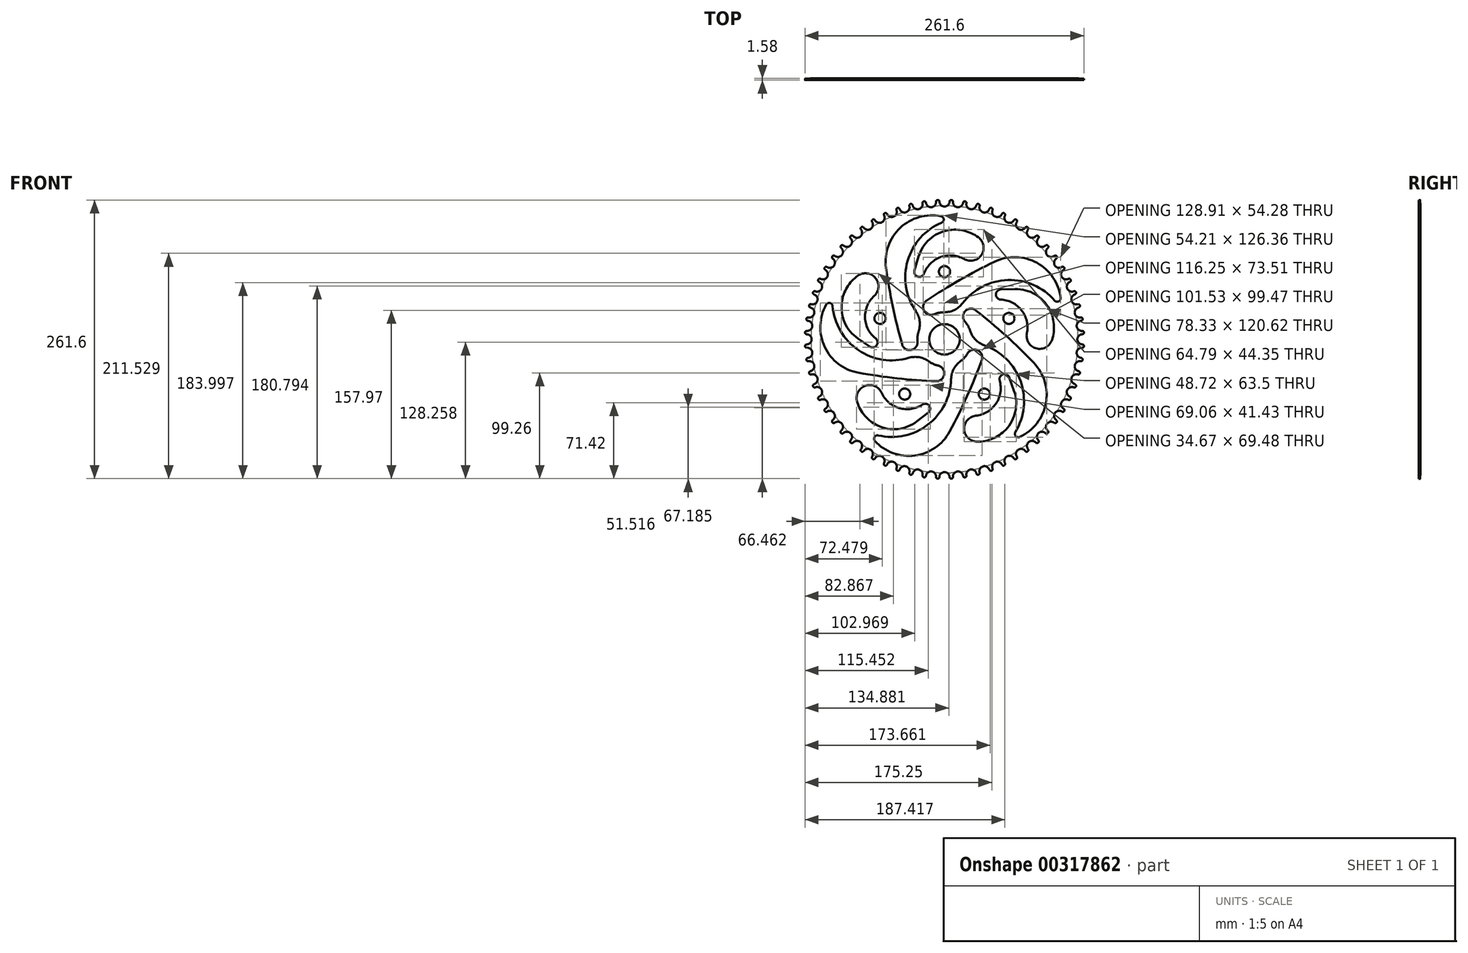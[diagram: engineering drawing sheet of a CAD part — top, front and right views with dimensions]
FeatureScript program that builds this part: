
annotation { "Feature Type Name" : "Feature", "Feature Type Description" : "" }
export const myFeature = defineFeature(function(context is Context, id is Id, definition is map)
    precondition{}
    {
        {
            var Q0;
            Q0=qCreatedBy(makeId("Front.planeOp"),FACE);
            var sketch = newSketch(context, id + "F0", { "sketchPlane" : qUnion([Q0])});
            skCircle(sketch, "E0", {"center": v(0, 0) * mm, "radius": 130.95 * mm});
            skCircle(sketch, "E1", {"center": v(0, 0) * mm, "radius": 14.29 * mm});
            skArc(sketch, "E2", {"start": v(-9.82, 23.42) * mm, "mid": v(-19.18, 26.74) * mm, "end": v(-16.8, 36.37) * mm});
            skArc(sketch, "E3", {"start": v(-16.8, 36.37) * mm, "mid": v(14.44, 55.74) * mm, "end": v(46.96, 72.85) * mm});
            skArc(sketch, "E4", {"start": v(46.96, 72.85) * mm, "mid": v(86.7, 71.8) * mm, "end": v(108.9, 38.83) * mm});
            skArc(sketch, "E5", {"start": v(108.9, 38.83) * mm, "mid": v(107.03, 35.54) * mm, "end": v(103.33, 36.37) * mm});
            skArc(sketch, "E6", {"start": v(103.33, 36.37) * mm, "mid": v(59.46, 55.67) * mm, "end": v(16.85, 33.75) * mm});
            skArc(sketch, "E7", {"start": v(16.85, 33.75) * mm, "mid": v(9.4, 27.6) * mm, "end": v(0, 25.4) * mm});
            skArc(sketch, "E8", {"start": v(0, 25.4) * mm, "mid": v(-5, 24.9) * mm, "end": v(-9.82, 23.42) * mm});
            skArc(sketch, "E9.1.0", {"start": v(-2.66, 109.51) * mm, "mid": v(-34.57, 73.76) * mm, "end": v(-26.89, 26.45) * mm});
            skArc(sketch, "E9.1.1", {"start": v(-26.89, 26.45) * mm, "mid": v(-23.34, 17.47) * mm, "end": v(-24.16, 7.85) * mm});
            skArc(sketch, "E9.1.2", {"start": v(-54.77, 67.17) * mm, "mid": v(-41.49, 104.64) * mm, "end": v(-3.27, 115.58) * mm});
            skArc(sketch, "E9.1.3", {"start": v(-25.31, -2.1) * mm, "mid": v(-31.36, -9.98) * mm, "end": v(-39.78, -4.73) * mm});
            skArc(sketch, "E9.1.4", {"start": v(-39.78, -4.73) * mm, "mid": v(-48.55, 30.96) * mm, "end": v(-54.77, 67.17) * mm});
            skArc(sketch, "E9.1.5", {"start": v(-3.27, 115.58) * mm, "mid": v(-0.73, 112.77) * mm, "end": v(-2.66, 109.51) * mm});
            skArc(sketch, "E9.1.6", {"start": v(-24.16, 7.85) * mm, "mid": v(-25.23, 2.93) * mm, "end": v(-25.31, -2.1) * mm});
            skArc(sketch, "E9.2.0", {"start": v(-104.98, 31.3) * mm, "mid": v(-80.83, -10.08) * mm, "end": v(-33.47, -17.4) * mm});
            skArc(sketch, "E9.2.1", {"start": v(-33.47, -17.4) * mm, "mid": v(-23.83, -16.8) * mm, "end": v(-14.93, -20.55) * mm});
            skArc(sketch, "E9.2.2", {"start": v(-80.8, -31.33) * mm, "mid": v(-112.34, -7.12) * mm, "end": v(-110.93, 32.6) * mm});
            skArc(sketch, "E9.2.3", {"start": v(-5.82, -24.72) * mm, "mid": v(-0.2, -32.9) * mm, "end": v(-7.8, -39.3) * mm});
            skArc(sketch, "E9.2.4", {"start": v(-7.8, -39.3) * mm, "mid": v(-44.44, -36.6) * mm, "end": v(-80.8, -31.33) * mm});
            skArc(sketch, "E9.2.5", {"start": v(-110.93, 32.6) * mm, "mid": v(-107.48, 34.16) * mm, "end": v(-104.98, 31.3) * mm});
            skArc(sketch, "E9.2.6", {"start": v(-14.93, -20.55) * mm, "mid": v(-10.58, -23.09) * mm, "end": v(-5.82, -24.72) * mm});
            skArc(sketch, "E9.3.0", {"start": v(-62.22, -90.16) * mm, "mid": v(-15.39, -79.99) * mm, "end": v(6.2, -37.2) * mm});
            skArc(sketch, "E9.3.1", {"start": v(6.2, -37.2) * mm, "mid": v(8.62, -27.86) * mm, "end": v(14.93, -20.55) * mm});
            skArc(sketch, "E9.3.2", {"start": v(4.83, -86.54) * mm, "mid": v(-27.94, -109.04) * mm, "end": v(-65.29, -95.43) * mm});
            skArc(sketch, "E9.3.3", {"start": v(21.71, -13.18) * mm, "mid": v(31.23, -10.35) * mm, "end": v(34.96, -19.56) * mm});
            skArc(sketch, "E9.3.4", {"start": v(34.96, -19.56) * mm, "mid": v(21.08, -53.58) * mm, "end": v(4.83, -86.54) * mm});
            skArc(sketch, "E9.3.5", {"start": v(-65.29, -95.43) * mm, "mid": v(-65.7, -91.66) * mm, "end": v(-62.22, -90.16) * mm});
            skArc(sketch, "E9.3.6", {"start": v(14.93, -20.55) * mm, "mid": v(18.69, -17.2) * mm, "end": v(21.71, -13.18) * mm});
            skArc(sketch, "E9.4.0", {"start": v(66.52, -87.03) * mm, "mid": v(71.32, -39.35) * mm, "end": v(37.3, -5.6) * mm});
            skArc(sketch, "E9.4.1", {"start": v(37.3, -5.6) * mm, "mid": v(29.16, -0.41) * mm, "end": v(24.16, 7.85) * mm});
            skArc(sketch, "E9.4.2", {"start": v(83.8, -22.15) * mm, "mid": v(95.07, -60.27) * mm, "end": v(70.58, -91.58) * mm});
            skArc(sketch, "E9.4.3", {"start": v(19.24, 16.58) * mm, "mid": v(19.5, 26.5) * mm, "end": v(29.4, 27.2) * mm});
            skArc(sketch, "E9.4.4", {"start": v(29.4, 27.2) * mm, "mid": v(57.47, 3.5) * mm, "end": v(83.8, -22.15) * mm});
            skArc(sketch, "E9.4.5", {"start": v(70.58, -91.58) * mm, "mid": v(66.87, -90.8) * mm, "end": v(66.52, -87.03) * mm});
            skArc(sketch, "E9.4.6", {"start": v(24.16, 7.85) * mm, "mid": v(22.13, 12.46) * mm, "end": v(19.24, 16.58) * mm});
            skArc(sketch, "E10", {"start": v(3.39, 102.34) * mm, "mid": v(-14.01, 93.86) * mm, "end": v(-24.34, 77.5) * mm});
            skArc(sketch, "E11", {"start": v(3.39, 102.34) * mm, "mid": v(18.22, 101.96) * mm, "end": v(31.69, 95.75) * mm});
            skArc(sketch, "E12", {"start": v(31.69, 95.75) * mm, "mid": v(34.69, 79.22) * mm, "end": v(18.36, 75.29) * mm});
            skArc(sketch, "E13", {"start": v(18.36, 75.29) * mm, "mid": v(-3.6, 77.18) * mm, "end": v(-19.22, 61.62) * mm});
            skArc(sketch, "E14", {"start": v(-19.22, 61.62) * mm, "mid": v(-25.11, 58.78) * mm, "end": v(-28.14, 64.57) * mm});
            skLineSegment(sketch, "E15", {"start": v(-28.14, 64.57) * mm, "end": v(-24.34, 77.5) * mm});
            skArc(sketch, "E16.1.1", {"start": v(-65.93, 40.72) * mm, "mid": v(-74.51, 20.42) * mm, "end": v(-64.55, 0.76) * mm});
            skArc(sketch, "E16.1.2", {"start": v(-81.27, 59.73) * mm, "mid": v(-64.63, 57.47) * mm, "end": v(-65.93, 40.72) * mm});
            skArc(sketch, "E16.1.3", {"start": v(-96.29, 34.85) * mm, "mid": v(-91.34, 48.83) * mm, "end": v(-81.27, 59.73) * mm});
            skArc(sketch, "E16.1.4", {"start": v(-96.29, 34.85) * mm, "mid": v(-93.6, 15.68) * mm, "end": v(-81.22, 0.8) * mm});
            skLineSegment(sketch, "E16.1.5", {"start": v(-70.1, -6.81) * mm, "end": v(-81.22, 0.8) * mm});
            skArc(sketch, "E16.1.6", {"start": v(-64.55, 0.76) * mm, "mid": v(-63.66, -5.72) * mm, "end": v(-70.1, -6.81) * mm});
            skArc(sketch, "E16.2.1", {"start": v(-59.1, -50.12) * mm, "mid": v(-42.45, -64.56) * mm, "end": v(-20.67, -61.15) * mm});
            skArc(sketch, "E16.2.2", {"start": v(-81.92, -58.84) * mm, "mid": v(-74.63, -43.7) * mm, "end": v(-59.1, -50.12) * mm});
            skArc(sketch, "E16.2.3", {"start": v(-62.9, -80.8) * mm, "mid": v(-74.67, -71.78) * mm, "end": v(-81.92, -58.84) * mm});
            skArc(sketch, "E16.2.4", {"start": v(-62.9, -80.8) * mm, "mid": v(-43.84, -84.17) * mm, "end": v(-25.85, -77) * mm});
            skLineSegment(sketch, "E16.2.5", {"start": v(-15.18, -68.78) * mm, "end": v(-25.85, -77) * mm});
            skArc(sketch, "E16.2.6", {"start": v(-20.67, -61.15) * mm, "mid": v(-14.24, -62.32) * mm, "end": v(-15.18, -68.78) * mm});
            skArc(sketch, "E16.3.1", {"start": v(29.4, -71.7) * mm, "mid": v(48.28, -60.32) * mm, "end": v(51.77, -38.55) * mm});
            skArc(sketch, "E16.3.2", {"start": v(30.64, -96.1) * mm, "mid": v(18.5, -84.48) * mm, "end": v(29.4, -71.7) * mm});
            skArc(sketch, "E16.3.3", {"start": v(57.41, -84.8) * mm, "mid": v(45.2, -93.2) * mm, "end": v(30.64, -96.1) * mm});
            skArc(sketch, "E16.3.4", {"start": v(57.41, -84.8) * mm, "mid": v(66.5, -67.7) * mm, "end": v(65.24, -48.38) * mm});
            skLineSegment(sketch, "E16.3.5", {"start": v(60.72, -35.7) * mm, "end": v(65.24, -48.38) * mm});
            skArc(sketch, "E16.3.6", {"start": v(51.77, -38.55) * mm, "mid": v(54.87, -32.8) * mm, "end": v(60.72, -35.7) * mm});
            skCircle(sketch, "E16.4.0", {"center": v(60.4, 19.62) * mm, "radius": 5.24 * mm});
            skArc(sketch, "E16.4.1", {"start": v(77.27, 5.8) * mm, "mid": v(72.28, 27.28) * mm, "end": v(52.66, 37.32) * mm});
            skArc(sketch, "E16.4.2", {"start": v(100.86, -0.55) * mm, "mid": v(86.06, -8.5) * mm, "end": v(77.27, 5.8) * mm});
            skArc(sketch, "E16.4.3", {"start": v(98.38, 28.4) * mm, "mid": v(102.6, 14.18) * mm, "end": v(100.86, -0.55) * mm});
            skArc(sketch, "E16.4.4", {"start": v(98.38, 28.4) * mm, "mid": v(84.94, 42.33) * mm, "end": v(66.18, 47.1) * mm});
            skLineSegment(sketch, "E16.4.5", {"start": v(52.71, 46.72) * mm, "end": v(66.18, 47.1) * mm});
            skArc(sketch, "E16.4.6", {"start": v(52.66, 37.32) * mm, "mid": v(48.15, 42.05) * mm, "end": v(52.71, 46.72) * mm});
            skArc(sketch, "E17", {"start": v(129.27, 4.76) * mm, "mid": v(125.86, -3.23) * mm, "end": v(134.1, -0.46) * mm});
            skArc(sketch, "E18", {"start": v(129.27, 4.76) * mm, "mid": v(130.82, 6.43) * mm, "end": v(129.12, 7.94) * mm});
            skLineSegment(sketch, "E19", {"start": v(129.12, 7.94) * mm, "end": v(137.96, 11.37) * mm});
            skLineSegment(sketch, "E20", {"start": v(137.96, 11.37) * mm, "end": v(139.02, 0) * mm});
            skLineSegment(sketch, "E21", {"start": v(139.02, 0) * mm, "end": v(134.1, -0.46) * mm});
            skLineSegment(sketch, "E22.1.0", {"start": v(127.72, 20.55) * mm, "end": v(136.19, 24.83) * mm});
            skLineSegment(sketch, "E22.1.1", {"start": v(136.19, 24.83) * mm, "end": v(138.35, 13.63) * mm});
            skLineSegment(sketch, "E22.1.2", {"start": v(138.35, 13.63) * mm, "end": v(133.5, 12.69) * mm});
            skArc(sketch, "E22.1.3", {"start": v(128.18, 17.4) * mm, "mid": v(129.56, 19.22) * mm, "end": v(127.72, 20.55) * mm});
            skArc(sketch, "E22.1.4", {"start": v(128.18, 17.4) * mm, "mid": v(125.58, 9.12) * mm, "end": v(133.5, 12.69) * mm});
            skLineSegment(sketch, "E22.2.0", {"start": v(125.09, 32.97) * mm, "end": v(133.1, 38.06) * mm});
            skLineSegment(sketch, "E22.2.1", {"start": v(133.1, 38.06) * mm, "end": v(136.35, 27.12) * mm});
            skLineSegment(sketch, "E22.2.2", {"start": v(136.35, 27.12) * mm, "end": v(131.61, 25.71) * mm});
            skArc(sketch, "E22.2.3", {"start": v(125.86, 29.9) * mm, "mid": v(127.05, 31.83) * mm, "end": v(125.09, 32.97) * mm});
            skArc(sketch, "E22.2.4", {"start": v(125.86, 29.9) * mm, "mid": v(124.08, 21.38) * mm, "end": v(131.61, 25.71) * mm});
            skLineSegment(sketch, "E22.3.0", {"start": v(121.25, 45.08) * mm, "end": v(128.72, 50.93) * mm});
            skLineSegment(sketch, "E22.3.1", {"start": v(128.72, 50.93) * mm, "end": v(133.04, 40.36) * mm});
            skLineSegment(sketch, "E22.3.2", {"start": v(133.04, 40.36) * mm, "end": v(128.46, 38.49) * mm});
            skArc(sketch, "E22.3.3", {"start": v(122.32, 42.08) * mm, "mid": v(123.32, 44.13) * mm, "end": v(121.25, 45.08) * mm});
            skArc(sketch, "E22.3.4", {"start": v(122.32, 42.08) * mm, "mid": v(121.38, 33.44) * mm, "end": v(128.46, 38.49) * mm});
            skLineSegment(sketch, "E22.4.0", {"start": v(116.25, 56.74) * mm, "end": v(123.11, 63.3) * mm});
            skLineSegment(sketch, "E22.4.1", {"start": v(123.11, 63.3) * mm, "end": v(128.44, 53.2) * mm});
            skLineSegment(sketch, "E22.4.2", {"start": v(128.44, 53.2) * mm, "end": v(124.07, 50.9) * mm});
            skArc(sketch, "E22.4.3", {"start": v(117.61, 53.87) * mm, "mid": v(118.4, 56) * mm, "end": v(116.25, 56.74) * mm});
            skArc(sketch, "E22.4.4", {"start": v(117.61, 53.87) * mm, "mid": v(117.52, 45.18) * mm, "end": v(124.07, 50.9) * mm});
            skLineSegment(sketch, "E22.5.0", {"start": v(110.13, 67.87) * mm, "end": v(116.32, 75.06) * mm});
            skLineSegment(sketch, "E22.5.1", {"start": v(116.32, 75.06) * mm, "end": v(122.6, 65.54) * mm});
            skLineSegment(sketch, "E22.5.2", {"start": v(122.6, 65.54) * mm, "end": v(118.48, 62.81) * mm});
            skArc(sketch, "E22.5.3", {"start": v(111.76, 65.14) * mm, "mid": v(112.34, 67.34) * mm, "end": v(110.13, 67.87) * mm});
            skArc(sketch, "E22.5.4", {"start": v(111.76, 65.14) * mm, "mid": v(112.53, 56.48) * mm, "end": v(118.48, 62.81) * mm});
            skLineSegment(sketch, "E22.6.0", {"start": v(102.95, 78.33) * mm, "end": v(108.4, 86.1) * mm});
            skLineSegment(sketch, "E22.6.1", {"start": v(108.4, 86.1) * mm, "end": v(115.6, 77.24) * mm});
            skLineSegment(sketch, "E22.6.2", {"start": v(115.6, 77.24) * mm, "end": v(111.76, 74.12) * mm});
            skArc(sketch, "E22.6.3", {"start": v(104.84, 75.78) * mm, "mid": v(105.2, 78.02) * mm, "end": v(102.95, 78.33) * mm});
            skArc(sketch, "E22.6.4", {"start": v(104.84, 75.78) * mm, "mid": v(106.45, 67.24) * mm, "end": v(111.76, 74.12) * mm});
            skLineSegment(sketch, "E22.7.0", {"start": v(94.77, 88.05) * mm, "end": v(99.44, 96.3) * mm});
            skLineSegment(sketch, "E22.7.1", {"start": v(99.44, 96.3) * mm, "end": v(107.47, 88.2) * mm});
            skLineSegment(sketch, "E22.7.2", {"start": v(107.47, 88.2) * mm, "end": v(103.95, 84.72) * mm});
            skArc(sketch, "E22.7.3", {"start": v(96.9, 85.7) * mm, "mid": v(97.04, 87.96) * mm, "end": v(94.77, 88.05) * mm});
            skArc(sketch, "E22.7.4", {"start": v(96.9, 85.7) * mm, "mid": v(99.35, 77.35) * mm, "end": v(103.95, 84.72) * mm});
            skLineSegment(sketch, "E22.8.0", {"start": v(85.69, 96.91) * mm, "end": v(89.52, 105.6) * mm});
            skLineSegment(sketch, "E22.8.1", {"start": v(89.52, 105.6) * mm, "end": v(98.3, 98.3) * mm});
            skLineSegment(sketch, "E22.8.2", {"start": v(98.3, 98.3) * mm, "end": v(95.15, 94.5) * mm});
            skArc(sketch, "E22.8.3", {"start": v(88.04, 94.78) * mm, "mid": v(87.96, 97.05) * mm, "end": v(85.69, 96.91) * mm});
            skArc(sketch, "E22.8.4", {"start": v(88.04, 94.78) * mm, "mid": v(91.29, 86.71) * mm, "end": v(95.15, 94.5) * mm});
            skLineSegment(sketch, "E22.9.0", {"start": v(75.78, 104.84) * mm, "end": v(78.74, 113.86) * mm});
            skLineSegment(sketch, "E22.9.1", {"start": v(78.74, 113.86) * mm, "end": v(88.2, 107.47) * mm});
            skLineSegment(sketch, "E22.9.2", {"start": v(88.2, 107.47) * mm, "end": v(85.43, 103.37) * mm});
            skArc(sketch, "E22.9.3", {"start": v(78.33, 102.95) * mm, "mid": v(78.02, 105.2) * mm, "end": v(75.78, 104.84) * mm});
            skArc(sketch, "E22.9.4", {"start": v(78.33, 102.95) * mm, "mid": v(82.35, 95.24) * mm, "end": v(85.43, 103.37) * mm});
            skLineSegment(sketch, "E22.10.0", {"start": v(65.13, 111.77) * mm, "end": v(67.2, 121.03) * mm});
            skLineSegment(sketch, "E22.10.1", {"start": v(67.2, 121.03) * mm, "end": v(77.24, 115.6) * mm});
            skLineSegment(sketch, "E22.10.2", {"start": v(77.24, 115.6) * mm, "end": v(74.88, 111.25) * mm});
            skArc(sketch, "E22.10.3", {"start": v(67.86, 110.13) * mm, "mid": v(67.33, 112.34) * mm, "end": v(65.13, 111.77) * mm});
            skArc(sketch, "E22.10.4", {"start": v(67.86, 110.13) * mm, "mid": v(72.62, 102.86) * mm, "end": v(74.88, 111.25) * mm});
            skLineSegment(sketch, "E22.11.0", {"start": v(53.87, 117.61) * mm, "end": v(55.01, 127.03) * mm});
            skLineSegment(sketch, "E22.11.1", {"start": v(55.01, 127.03) * mm, "end": v(65.54, 122.6) * mm});
            skLineSegment(sketch, "E22.11.2", {"start": v(65.54, 122.6) * mm, "end": v(63.62, 118.05) * mm});
            skArc(sketch, "E22.11.3", {"start": v(56.74, 116.25) * mm, "mid": v(56, 118.4) * mm, "end": v(53.87, 117.61) * mm});
            skArc(sketch, "E22.11.4", {"start": v(56.74, 116.25) * mm, "mid": v(62.18, 109.48) * mm, "end": v(63.62, 118.05) * mm});
            skLineSegment(sketch, "E22.12.0", {"start": v(42.08, 122.33) * mm, "end": v(42.3, 131.81) * mm});
            skLineSegment(sketch, "E22.12.1", {"start": v(42.3, 131.81) * mm, "end": v(53.2, 128.44) * mm});
            skLineSegment(sketch, "E22.12.2", {"start": v(53.2, 128.44) * mm, "end": v(51.74, 123.72) * mm});
            skArc(sketch, "E22.12.3", {"start": v(45.07, 121.26) * mm, "mid": v(44.12, 123.32) * mm, "end": v(42.08, 122.33) * mm});
            skArc(sketch, "E22.12.4", {"start": v(45.07, 121.26) * mm, "mid": v(51.15, 115.05) * mm, "end": v(51.74, 123.72) * mm});
            skLineSegment(sketch, "E22.13.0", {"start": v(29.89, 125.86) * mm, "end": v(29.17, 135.32) * mm});
            skLineSegment(sketch, "E22.13.1", {"start": v(29.17, 135.32) * mm, "end": v(40.36, 133.04) * mm});
            skLineSegment(sketch, "E22.13.2", {"start": v(40.36, 133.04) * mm, "end": v(39.37, 128.2) * mm});
            skArc(sketch, "E22.13.3", {"start": v(32.97, 125.09) * mm, "mid": v(31.82, 127.05) * mm, "end": v(29.89, 125.86) * mm});
            skArc(sketch, "E22.13.4", {"start": v(32.97, 125.09) * mm, "mid": v(39.63, 119.5) * mm, "end": v(39.37, 128.2) * mm});
            skLineSegment(sketch, "E22.14.0", {"start": v(17.4, 128.18) * mm, "end": v(15.77, 137.53) * mm});
            skLineSegment(sketch, "E22.14.1", {"start": v(15.77, 137.53) * mm, "end": v(27.12, 136.35) * mm});
            skLineSegment(sketch, "E22.14.2", {"start": v(27.12, 136.35) * mm, "end": v(26.61, 131.44) * mm});
            skArc(sketch, "E22.14.3", {"start": v(20.55, 127.72) * mm, "mid": v(19.22, 129.56) * mm, "end": v(17.4, 128.18) * mm});
            skArc(sketch, "E22.14.4", {"start": v(20.55, 127.72) * mm, "mid": v(27.73, 122.82) * mm, "end": v(26.61, 131.44) * mm});
            skLineSegment(sketch, "E22.15.0", {"start": v(4.76, 129.27) * mm, "end": v(2.21, 138.41) * mm});
            skLineSegment(sketch, "E22.15.1", {"start": v(2.21, 138.41) * mm, "end": v(13.63, 138.35) * mm});
            skLineSegment(sketch, "E22.15.2", {"start": v(13.63, 138.35) * mm, "end": v(13.6, 133.41) * mm});
            skArc(sketch, "E22.15.3", {"start": v(7.93, 129.12) * mm, "mid": v(6.42, 130.82) * mm, "end": v(4.76, 129.27) * mm});
            skArc(sketch, "E22.15.4", {"start": v(7.93, 129.12) * mm, "mid": v(15.56, 124.94) * mm, "end": v(13.6, 133.41) * mm});
            skLineSegment(sketch, "E22.16.0", {"start": v(-7.94, 129.12) * mm, "end": v(-11.37, 137.96) * mm});
            skLineSegment(sketch, "E22.16.1", {"start": v(-11.37, 137.96) * mm, "end": v(0, 139.02) * mm});
            skLineSegment(sketch, "E22.16.2", {"start": v(0, 139.02) * mm, "end": v(0.46, 134.1) * mm});
            skArc(sketch, "E22.16.3", {"start": v(-4.76, 129.27) * mm, "mid": v(-6.43, 130.82) * mm, "end": v(-7.94, 129.12) * mm});
            skArc(sketch, "E22.16.4", {"start": v(-4.76, 129.27) * mm, "mid": v(3.23, 125.86) * mm, "end": v(0.46, 134.1) * mm});
            skLineSegment(sketch, "E22.17.0", {"start": v(-20.55, 127.72) * mm, "end": v(-24.83, 136.19) * mm});
            skLineSegment(sketch, "E22.17.1", {"start": v(-24.83, 136.19) * mm, "end": v(-13.63, 138.35) * mm});
            skLineSegment(sketch, "E22.17.2", {"start": v(-13.63, 138.35) * mm, "end": v(-12.69, 133.5) * mm});
            skArc(sketch, "E22.17.3", {"start": v(-17.4, 128.18) * mm, "mid": v(-19.22, 129.56) * mm, "end": v(-20.55, 127.72) * mm});
            skArc(sketch, "E22.17.4", {"start": v(-17.4, 128.18) * mm, "mid": v(-9.12, 125.58) * mm, "end": v(-12.69, 133.5) * mm});
            skLineSegment(sketch, "E22.18.0", {"start": v(-32.97, 125.09) * mm, "end": v(-38.06, 133.1) * mm});
            skLineSegment(sketch, "E22.18.1", {"start": v(-38.06, 133.1) * mm, "end": v(-27.12, 136.35) * mm});
            skLineSegment(sketch, "E22.18.2", {"start": v(-27.12, 136.35) * mm, "end": v(-25.71, 131.61) * mm});
            skArc(sketch, "E22.18.3", {"start": v(-29.9, 125.86) * mm, "mid": v(-31.83, 127.05) * mm, "end": v(-32.97, 125.09) * mm});
            skArc(sketch, "E22.18.4", {"start": v(-29.9, 125.86) * mm, "mid": v(-21.38, 124.08) * mm, "end": v(-25.71, 131.61) * mm});
            skLineSegment(sketch, "E22.19.0", {"start": v(-45.08, 121.25) * mm, "end": v(-50.93, 128.72) * mm});
            skLineSegment(sketch, "E22.19.1", {"start": v(-50.93, 128.72) * mm, "end": v(-40.36, 133.04) * mm});
            skLineSegment(sketch, "E22.19.2", {"start": v(-40.36, 133.04) * mm, "end": v(-38.49, 128.46) * mm});
            skArc(sketch, "E22.19.3", {"start": v(-42.08, 122.32) * mm, "mid": v(-44.13, 123.32) * mm, "end": v(-45.08, 121.25) * mm});
            skArc(sketch, "E22.19.4", {"start": v(-42.08, 122.32) * mm, "mid": v(-33.44, 121.38) * mm, "end": v(-38.49, 128.46) * mm});
            skLineSegment(sketch, "E22.20.0", {"start": v(-56.74, 116.25) * mm, "end": v(-63.3, 123.11) * mm});
            skLineSegment(sketch, "E22.20.1", {"start": v(-63.3, 123.11) * mm, "end": v(-53.2, 128.44) * mm});
            skLineSegment(sketch, "E22.20.2", {"start": v(-53.2, 128.44) * mm, "end": v(-50.9, 124.07) * mm});
            skArc(sketch, "E22.20.3", {"start": v(-53.87, 117.61) * mm, "mid": v(-56, 118.4) * mm, "end": v(-56.74, 116.25) * mm});
            skArc(sketch, "E22.20.4", {"start": v(-53.87, 117.61) * mm, "mid": v(-45.18, 117.52) * mm, "end": v(-50.9, 124.07) * mm});
            skLineSegment(sketch, "E22.21.0", {"start": v(-67.87, 110.13) * mm, "end": v(-75.06, 116.32) * mm});
            skLineSegment(sketch, "E22.21.1", {"start": v(-75.06, 116.32) * mm, "end": v(-65.54, 122.6) * mm});
            skLineSegment(sketch, "E22.21.2", {"start": v(-65.54, 122.6) * mm, "end": v(-62.81, 118.48) * mm});
            skArc(sketch, "E22.21.3", {"start": v(-65.14, 111.76) * mm, "mid": v(-67.34, 112.34) * mm, "end": v(-67.87, 110.13) * mm});
            skArc(sketch, "E22.21.4", {"start": v(-65.14, 111.76) * mm, "mid": v(-56.48, 112.53) * mm, "end": v(-62.81, 118.48) * mm});
            skLineSegment(sketch, "E22.22.0", {"start": v(-78.33, 102.95) * mm, "end": v(-86.1, 108.4) * mm});
            skLineSegment(sketch, "E22.22.1", {"start": v(-86.1, 108.4) * mm, "end": v(-77.24, 115.6) * mm});
            skLineSegment(sketch, "E22.22.2", {"start": v(-77.24, 115.6) * mm, "end": v(-74.12, 111.76) * mm});
            skArc(sketch, "E22.22.3", {"start": v(-75.78, 104.84) * mm, "mid": v(-78.02, 105.2) * mm, "end": v(-78.33, 102.95) * mm});
            skArc(sketch, "E22.22.4", {"start": v(-75.78, 104.84) * mm, "mid": v(-67.24, 106.45) * mm, "end": v(-74.12, 111.76) * mm});
            skLineSegment(sketch, "E22.23.0", {"start": v(-88.05, 94.77) * mm, "end": v(-96.3, 99.44) * mm});
            skLineSegment(sketch, "E22.23.1", {"start": v(-96.3, 99.44) * mm, "end": v(-88.2, 107.47) * mm});
            skLineSegment(sketch, "E22.23.2", {"start": v(-88.2, 107.47) * mm, "end": v(-84.72, 103.95) * mm});
            skArc(sketch, "E22.23.3", {"start": v(-85.7, 96.9) * mm, "mid": v(-87.96, 97.04) * mm, "end": v(-88.05, 94.77) * mm});
            skArc(sketch, "E22.23.4", {"start": v(-85.7, 96.9) * mm, "mid": v(-77.35, 99.35) * mm, "end": v(-84.72, 103.95) * mm});
            skLineSegment(sketch, "E22.24.0", {"start": v(-96.91, 85.69) * mm, "end": v(-105.6, 89.52) * mm});
            skLineSegment(sketch, "E22.24.1", {"start": v(-105.6, 89.52) * mm, "end": v(-98.3, 98.3) * mm});
            skLineSegment(sketch, "E22.24.2", {"start": v(-98.3, 98.3) * mm, "end": v(-94.5, 95.15) * mm});
            skArc(sketch, "E22.24.3", {"start": v(-94.78, 88.04) * mm, "mid": v(-97.05, 87.96) * mm, "end": v(-96.91, 85.69) * mm});
            skArc(sketch, "E22.24.4", {"start": v(-94.78, 88.04) * mm, "mid": v(-86.71, 91.29) * mm, "end": v(-94.5, 95.15) * mm});
            skLineSegment(sketch, "E22.25.0", {"start": v(-104.84, 75.78) * mm, "end": v(-113.86, 78.74) * mm});
            skLineSegment(sketch, "E22.25.1", {"start": v(-113.86, 78.74) * mm, "end": v(-107.47, 88.2) * mm});
            skLineSegment(sketch, "E22.25.2", {"start": v(-107.47, 88.2) * mm, "end": v(-103.37, 85.43) * mm});
            skArc(sketch, "E22.25.3", {"start": v(-102.95, 78.33) * mm, "mid": v(-105.2, 78.02) * mm, "end": v(-104.84, 75.78) * mm});
            skArc(sketch, "E22.25.4", {"start": v(-102.95, 78.33) * mm, "mid": v(-95.24, 82.35) * mm, "end": v(-103.37, 85.43) * mm});
            skLineSegment(sketch, "E22.26.0", {"start": v(-111.77, 65.13) * mm, "end": v(-121.03, 67.2) * mm});
            skLineSegment(sketch, "E22.26.1", {"start": v(-121.03, 67.2) * mm, "end": v(-115.6, 77.24) * mm});
            skLineSegment(sketch, "E22.26.2", {"start": v(-115.6, 77.24) * mm, "end": v(-111.25, 74.88) * mm});
            skArc(sketch, "E22.26.3", {"start": v(-110.13, 67.86) * mm, "mid": v(-112.34, 67.33) * mm, "end": v(-111.77, 65.13) * mm});
            skArc(sketch, "E22.26.4", {"start": v(-110.13, 67.86) * mm, "mid": v(-102.86, 72.62) * mm, "end": v(-111.25, 74.88) * mm});
            skLineSegment(sketch, "E22.27.0", {"start": v(-117.61, 53.87) * mm, "end": v(-127.03, 55.01) * mm});
            skLineSegment(sketch, "E22.27.1", {"start": v(-127.03, 55.01) * mm, "end": v(-122.6, 65.54) * mm});
            skLineSegment(sketch, "E22.27.2", {"start": v(-122.6, 65.54) * mm, "end": v(-118.05, 63.62) * mm});
            skArc(sketch, "E22.27.3", {"start": v(-116.25, 56.74) * mm, "mid": v(-118.4, 56) * mm, "end": v(-117.61, 53.87) * mm});
            skArc(sketch, "E22.27.4", {"start": v(-116.25, 56.74) * mm, "mid": v(-109.48, 62.18) * mm, "end": v(-118.05, 63.62) * mm});
            skLineSegment(sketch, "E22.28.0", {"start": v(-122.33, 42.08) * mm, "end": v(-131.81, 42.3) * mm});
            skLineSegment(sketch, "E22.28.1", {"start": v(-131.81, 42.3) * mm, "end": v(-128.44, 53.2) * mm});
            skLineSegment(sketch, "E22.28.2", {"start": v(-128.44, 53.2) * mm, "end": v(-123.72, 51.74) * mm});
            skArc(sketch, "E22.28.3", {"start": v(-121.26, 45.07) * mm, "mid": v(-123.32, 44.12) * mm, "end": v(-122.33, 42.08) * mm});
            skArc(sketch, "E22.28.4", {"start": v(-121.26, 45.07) * mm, "mid": v(-115.05, 51.15) * mm, "end": v(-123.72, 51.74) * mm});
            skLineSegment(sketch, "E22.29.0", {"start": v(-125.86, 29.89) * mm, "end": v(-135.32, 29.17) * mm});
            skLineSegment(sketch, "E22.29.1", {"start": v(-135.32, 29.17) * mm, "end": v(-133.04, 40.36) * mm});
            skLineSegment(sketch, "E22.29.2", {"start": v(-133.04, 40.36) * mm, "end": v(-128.2, 39.37) * mm});
            skArc(sketch, "E22.29.3", {"start": v(-125.09, 32.97) * mm, "mid": v(-127.05, 31.82) * mm, "end": v(-125.86, 29.89) * mm});
            skArc(sketch, "E22.29.4", {"start": v(-125.09, 32.97) * mm, "mid": v(-119.5, 39.63) * mm, "end": v(-128.2, 39.37) * mm});
            skLineSegment(sketch, "E22.30.0", {"start": v(-128.18, 17.4) * mm, "end": v(-137.53, 15.77) * mm});
            skLineSegment(sketch, "E22.30.1", {"start": v(-137.53, 15.77) * mm, "end": v(-136.35, 27.12) * mm});
            skLineSegment(sketch, "E22.30.2", {"start": v(-136.35, 27.12) * mm, "end": v(-131.44, 26.61) * mm});
            skArc(sketch, "E22.30.3", {"start": v(-127.72, 20.55) * mm, "mid": v(-129.56, 19.22) * mm, "end": v(-128.18, 17.4) * mm});
            skArc(sketch, "E22.30.4", {"start": v(-127.72, 20.55) * mm, "mid": v(-122.82, 27.73) * mm, "end": v(-131.44, 26.61) * mm});
            skLineSegment(sketch, "E22.31.0", {"start": v(-129.27, 4.76) * mm, "end": v(-138.41, 2.21) * mm});
            skLineSegment(sketch, "E22.31.1", {"start": v(-138.41, 2.21) * mm, "end": v(-138.35, 13.63) * mm});
            skLineSegment(sketch, "E22.31.2", {"start": v(-138.35, 13.63) * mm, "end": v(-133.41, 13.6) * mm});
            skArc(sketch, "E22.31.3", {"start": v(-129.12, 7.93) * mm, "mid": v(-130.82, 6.42) * mm, "end": v(-129.27, 4.76) * mm});
            skArc(sketch, "E22.31.4", {"start": v(-129.12, 7.93) * mm, "mid": v(-124.94, 15.56) * mm, "end": v(-133.41, 13.6) * mm});
            skLineSegment(sketch, "E22.32.0", {"start": v(-129.12, -7.94) * mm, "end": v(-137.96, -11.37) * mm});
            skLineSegment(sketch, "E22.32.1", {"start": v(-137.96, -11.37) * mm, "end": v(-139.02, 0) * mm});
            skLineSegment(sketch, "E22.32.2", {"start": v(-139.02, 0) * mm, "end": v(-134.1, 0.46) * mm});
            skArc(sketch, "E22.32.3", {"start": v(-129.27, -4.76) * mm, "mid": v(-130.82, -6.43) * mm, "end": v(-129.12, -7.94) * mm});
            skArc(sketch, "E22.32.4", {"start": v(-129.27, -4.76) * mm, "mid": v(-125.86, 3.23) * mm, "end": v(-134.1, 0.46) * mm});
            skLineSegment(sketch, "E22.33.0", {"start": v(-127.72, -20.55) * mm, "end": v(-136.19, -24.83) * mm});
            skLineSegment(sketch, "E22.33.1", {"start": v(-136.19, -24.83) * mm, "end": v(-138.35, -13.63) * mm});
            skLineSegment(sketch, "E22.33.2", {"start": v(-138.35, -13.63) * mm, "end": v(-133.5, -12.69) * mm});
            skArc(sketch, "E22.33.3", {"start": v(-128.18, -17.4) * mm, "mid": v(-129.56, -19.22) * mm, "end": v(-127.72, -20.55) * mm});
            skArc(sketch, "E22.33.4", {"start": v(-128.18, -17.4) * mm, "mid": v(-125.58, -9.12) * mm, "end": v(-133.5, -12.69) * mm});
            skLineSegment(sketch, "E22.34.0", {"start": v(-125.09, -32.97) * mm, "end": v(-133.1, -38.06) * mm});
            skLineSegment(sketch, "E22.34.1", {"start": v(-133.1, -38.06) * mm, "end": v(-136.35, -27.12) * mm});
            skLineSegment(sketch, "E22.34.2", {"start": v(-136.35, -27.12) * mm, "end": v(-131.61, -25.71) * mm});
            skArc(sketch, "E22.34.3", {"start": v(-125.86, -29.9) * mm, "mid": v(-127.05, -31.83) * mm, "end": v(-125.09, -32.97) * mm});
            skArc(sketch, "E22.34.4", {"start": v(-125.86, -29.9) * mm, "mid": v(-124.08, -21.38) * mm, "end": v(-131.61, -25.71) * mm});
            skLineSegment(sketch, "E22.35.0", {"start": v(-121.25, -45.08) * mm, "end": v(-128.72, -50.93) * mm});
            skLineSegment(sketch, "E22.35.1", {"start": v(-128.72, -50.93) * mm, "end": v(-133.04, -40.36) * mm});
            skLineSegment(sketch, "E22.35.2", {"start": v(-133.04, -40.36) * mm, "end": v(-128.46, -38.49) * mm});
            skArc(sketch, "E22.35.3", {"start": v(-122.32, -42.08) * mm, "mid": v(-123.32, -44.13) * mm, "end": v(-121.25, -45.08) * mm});
            skArc(sketch, "E22.35.4", {"start": v(-122.32, -42.08) * mm, "mid": v(-121.38, -33.44) * mm, "end": v(-128.46, -38.49) * mm});
            skLineSegment(sketch, "E22.36.0", {"start": v(-116.25, -56.74) * mm, "end": v(-123.11, -63.3) * mm});
            skLineSegment(sketch, "E22.36.1", {"start": v(-123.11, -63.3) * mm, "end": v(-128.44, -53.2) * mm});
            skLineSegment(sketch, "E22.36.2", {"start": v(-128.44, -53.2) * mm, "end": v(-124.07, -50.9) * mm});
            skArc(sketch, "E22.36.3", {"start": v(-117.61, -53.87) * mm, "mid": v(-118.4, -56) * mm, "end": v(-116.25, -56.74) * mm});
            skArc(sketch, "E22.36.4", {"start": v(-117.61, -53.87) * mm, "mid": v(-117.52, -45.18) * mm, "end": v(-124.07, -50.9) * mm});
            skLineSegment(sketch, "E22.37.0", {"start": v(-110.13, -67.87) * mm, "end": v(-116.32, -75.06) * mm});
            skLineSegment(sketch, "E22.37.1", {"start": v(-116.32, -75.06) * mm, "end": v(-122.6, -65.54) * mm});
            skLineSegment(sketch, "E22.37.2", {"start": v(-122.6, -65.54) * mm, "end": v(-118.48, -62.81) * mm});
            skArc(sketch, "E22.37.3", {"start": v(-111.76, -65.14) * mm, "mid": v(-112.34, -67.34) * mm, "end": v(-110.13, -67.87) * mm});
            skArc(sketch, "E22.37.4", {"start": v(-111.76, -65.14) * mm, "mid": v(-112.53, -56.48) * mm, "end": v(-118.48, -62.81) * mm});
            skLineSegment(sketch, "E22.38.0", {"start": v(-102.95, -78.33) * mm, "end": v(-108.4, -86.1) * mm});
            skLineSegment(sketch, "E22.38.1", {"start": v(-108.4, -86.1) * mm, "end": v(-115.6, -77.24) * mm});
            skLineSegment(sketch, "E22.38.2", {"start": v(-115.6, -77.24) * mm, "end": v(-111.76, -74.12) * mm});
            skArc(sketch, "E22.38.3", {"start": v(-104.84, -75.78) * mm, "mid": v(-105.2, -78.02) * mm, "end": v(-102.95, -78.33) * mm});
            skArc(sketch, "E22.38.4", {"start": v(-104.84, -75.78) * mm, "mid": v(-106.45, -67.24) * mm, "end": v(-111.76, -74.12) * mm});
            skLineSegment(sketch, "E22.39.0", {"start": v(-94.77, -88.05) * mm, "end": v(-99.44, -96.3) * mm});
            skLineSegment(sketch, "E22.39.1", {"start": v(-99.44, -96.3) * mm, "end": v(-107.47, -88.2) * mm});
            skLineSegment(sketch, "E22.39.2", {"start": v(-107.47, -88.2) * mm, "end": v(-103.95, -84.72) * mm});
            skArc(sketch, "E22.39.3", {"start": v(-96.9, -85.7) * mm, "mid": v(-97.04, -87.96) * mm, "end": v(-94.77, -88.05) * mm});
            skArc(sketch, "E22.39.4", {"start": v(-96.9, -85.7) * mm, "mid": v(-99.35, -77.35) * mm, "end": v(-103.95, -84.72) * mm});
            skLineSegment(sketch, "E22.40.0", {"start": v(-85.69, -96.91) * mm, "end": v(-89.52, -105.6) * mm});
            skLineSegment(sketch, "E22.40.1", {"start": v(-89.52, -105.6) * mm, "end": v(-98.3, -98.3) * mm});
            skLineSegment(sketch, "E22.40.2", {"start": v(-98.3, -98.3) * mm, "end": v(-95.15, -94.5) * mm});
            skArc(sketch, "E22.40.3", {"start": v(-88.04, -94.78) * mm, "mid": v(-87.96, -97.05) * mm, "end": v(-85.69, -96.91) * mm});
            skArc(sketch, "E22.40.4", {"start": v(-88.04, -94.78) * mm, "mid": v(-91.29, -86.71) * mm, "end": v(-95.15, -94.5) * mm});
            skLineSegment(sketch, "E22.41.0", {"start": v(-75.78, -104.84) * mm, "end": v(-78.74, -113.86) * mm});
            skLineSegment(sketch, "E22.41.1", {"start": v(-78.74, -113.86) * mm, "end": v(-88.2, -107.47) * mm});
            skLineSegment(sketch, "E22.41.2", {"start": v(-88.2, -107.47) * mm, "end": v(-85.43, -103.37) * mm});
            skArc(sketch, "E22.41.3", {"start": v(-78.33, -102.95) * mm, "mid": v(-78.02, -105.2) * mm, "end": v(-75.78, -104.84) * mm});
            skArc(sketch, "E22.41.4", {"start": v(-78.33, -102.95) * mm, "mid": v(-82.35, -95.24) * mm, "end": v(-85.43, -103.37) * mm});
            skLineSegment(sketch, "E22.42.0", {"start": v(-65.13, -111.77) * mm, "end": v(-67.2, -121.03) * mm});
            skLineSegment(sketch, "E22.42.1", {"start": v(-67.2, -121.03) * mm, "end": v(-77.24, -115.6) * mm});
            skLineSegment(sketch, "E22.42.2", {"start": v(-77.24, -115.6) * mm, "end": v(-74.88, -111.25) * mm});
            skArc(sketch, "E22.42.3", {"start": v(-67.86, -110.13) * mm, "mid": v(-67.33, -112.34) * mm, "end": v(-65.13, -111.77) * mm});
            skArc(sketch, "E22.42.4", {"start": v(-67.86, -110.13) * mm, "mid": v(-72.62, -102.86) * mm, "end": v(-74.88, -111.25) * mm});
            skLineSegment(sketch, "E22.43.0", {"start": v(-53.87, -117.61) * mm, "end": v(-55.01, -127.03) * mm});
            skLineSegment(sketch, "E22.43.1", {"start": v(-55.01, -127.03) * mm, "end": v(-65.54, -122.6) * mm});
            skLineSegment(sketch, "E22.43.2", {"start": v(-65.54, -122.6) * mm, "end": v(-63.62, -118.05) * mm});
            skArc(sketch, "E22.43.3", {"start": v(-56.74, -116.25) * mm, "mid": v(-56, -118.4) * mm, "end": v(-53.87, -117.61) * mm});
            skArc(sketch, "E22.43.4", {"start": v(-56.74, -116.25) * mm, "mid": v(-62.18, -109.48) * mm, "end": v(-63.62, -118.05) * mm});
            skLineSegment(sketch, "E22.44.0", {"start": v(-42.08, -122.33) * mm, "end": v(-42.3, -131.81) * mm});
            skLineSegment(sketch, "E22.44.1", {"start": v(-42.3, -131.81) * mm, "end": v(-53.2, -128.44) * mm});
            skLineSegment(sketch, "E22.44.2", {"start": v(-53.2, -128.44) * mm, "end": v(-51.74, -123.72) * mm});
            skArc(sketch, "E22.44.3", {"start": v(-45.07, -121.26) * mm, "mid": v(-44.12, -123.32) * mm, "end": v(-42.08, -122.33) * mm});
            skArc(sketch, "E22.44.4", {"start": v(-45.07, -121.26) * mm, "mid": v(-51.15, -115.05) * mm, "end": v(-51.74, -123.72) * mm});
            skLineSegment(sketch, "E22.45.0", {"start": v(-29.89, -125.86) * mm, "end": v(-29.17, -135.32) * mm});
            skLineSegment(sketch, "E22.45.1", {"start": v(-29.17, -135.32) * mm, "end": v(-40.36, -133.04) * mm});
            skLineSegment(sketch, "E22.45.2", {"start": v(-40.36, -133.04) * mm, "end": v(-39.37, -128.2) * mm});
            skArc(sketch, "E22.45.3", {"start": v(-32.97, -125.09) * mm, "mid": v(-31.82, -127.05) * mm, "end": v(-29.89, -125.86) * mm});
            skArc(sketch, "E22.45.4", {"start": v(-32.97, -125.09) * mm, "mid": v(-39.63, -119.5) * mm, "end": v(-39.37, -128.2) * mm});
            skLineSegment(sketch, "E22.46.0", {"start": v(-17.4, -128.18) * mm, "end": v(-15.77, -137.53) * mm});
            skLineSegment(sketch, "E22.46.1", {"start": v(-15.77, -137.53) * mm, "end": v(-27.12, -136.35) * mm});
            skLineSegment(sketch, "E22.46.2", {"start": v(-27.12, -136.35) * mm, "end": v(-26.61, -131.44) * mm});
            skArc(sketch, "E22.46.3", {"start": v(-20.55, -127.72) * mm, "mid": v(-19.22, -129.56) * mm, "end": v(-17.4, -128.18) * mm});
            skArc(sketch, "E22.46.4", {"start": v(-20.55, -127.72) * mm, "mid": v(-27.73, -122.82) * mm, "end": v(-26.61, -131.44) * mm});
            skLineSegment(sketch, "E22.47.0", {"start": v(-4.76, -129.27) * mm, "end": v(-2.21, -138.41) * mm});
            skLineSegment(sketch, "E22.47.1", {"start": v(-2.21, -138.41) * mm, "end": v(-13.63, -138.35) * mm});
            skLineSegment(sketch, "E22.47.2", {"start": v(-13.63, -138.35) * mm, "end": v(-13.6, -133.41) * mm});
            skArc(sketch, "E22.47.3", {"start": v(-7.93, -129.12) * mm, "mid": v(-6.42, -130.82) * mm, "end": v(-4.76, -129.27) * mm});
            skArc(sketch, "E22.47.4", {"start": v(-7.93, -129.12) * mm, "mid": v(-15.56, -124.94) * mm, "end": v(-13.6, -133.41) * mm});
            skLineSegment(sketch, "E22.48.0", {"start": v(7.94, -129.12) * mm, "end": v(11.37, -137.96) * mm});
            skLineSegment(sketch, "E22.48.1", {"start": v(11.37, -137.96) * mm, "end": v(0, -139.02) * mm});
            skLineSegment(sketch, "E22.48.2", {"start": v(0, -139.02) * mm, "end": v(-0.46, -134.1) * mm});
            skArc(sketch, "E22.48.3", {"start": v(4.76, -129.27) * mm, "mid": v(6.43, -130.82) * mm, "end": v(7.94, -129.12) * mm});
            skArc(sketch, "E22.48.4", {"start": v(4.76, -129.27) * mm, "mid": v(-3.23, -125.86) * mm, "end": v(-0.46, -134.1) * mm});
            skLineSegment(sketch, "E22.49.0", {"start": v(20.55, -127.72) * mm, "end": v(24.83, -136.19) * mm});
            skLineSegment(sketch, "E22.49.1", {"start": v(24.83, -136.19) * mm, "end": v(13.63, -138.35) * mm});
            skLineSegment(sketch, "E22.49.2", {"start": v(13.63, -138.35) * mm, "end": v(12.69, -133.5) * mm});
            skArc(sketch, "E22.49.3", {"start": v(17.4, -128.18) * mm, "mid": v(19.22, -129.56) * mm, "end": v(20.55, -127.72) * mm});
            skArc(sketch, "E22.49.4", {"start": v(17.4, -128.18) * mm, "mid": v(9.12, -125.58) * mm, "end": v(12.69, -133.5) * mm});
            skLineSegment(sketch, "E22.50.0", {"start": v(32.97, -125.09) * mm, "end": v(38.06, -133.1) * mm});
            skLineSegment(sketch, "E22.50.1", {"start": v(38.06, -133.1) * mm, "end": v(27.12, -136.35) * mm});
            skLineSegment(sketch, "E22.50.2", {"start": v(27.12, -136.35) * mm, "end": v(25.71, -131.61) * mm});
            skArc(sketch, "E22.50.3", {"start": v(29.9, -125.86) * mm, "mid": v(31.83, -127.05) * mm, "end": v(32.97, -125.09) * mm});
            skArc(sketch, "E22.50.4", {"start": v(29.9, -125.86) * mm, "mid": v(21.38, -124.08) * mm, "end": v(25.71, -131.61) * mm});
            skLineSegment(sketch, "E22.51.0", {"start": v(45.08, -121.25) * mm, "end": v(50.93, -128.72) * mm});
            skLineSegment(sketch, "E22.51.1", {"start": v(50.93, -128.72) * mm, "end": v(40.36, -133.04) * mm});
            skLineSegment(sketch, "E22.51.2", {"start": v(40.36, -133.04) * mm, "end": v(38.49, -128.46) * mm});
            skArc(sketch, "E22.51.3", {"start": v(42.08, -122.32) * mm, "mid": v(44.13, -123.32) * mm, "end": v(45.08, -121.25) * mm});
            skArc(sketch, "E22.51.4", {"start": v(42.08, -122.32) * mm, "mid": v(33.44, -121.38) * mm, "end": v(38.49, -128.46) * mm});
            skLineSegment(sketch, "E22.52.0", {"start": v(56.74, -116.25) * mm, "end": v(63.3, -123.11) * mm});
            skLineSegment(sketch, "E22.52.1", {"start": v(63.3, -123.11) * mm, "end": v(53.2, -128.44) * mm});
            skLineSegment(sketch, "E22.52.2", {"start": v(53.2, -128.44) * mm, "end": v(50.9, -124.07) * mm});
            skArc(sketch, "E22.52.3", {"start": v(53.87, -117.61) * mm, "mid": v(56, -118.4) * mm, "end": v(56.74, -116.25) * mm});
            skArc(sketch, "E22.52.4", {"start": v(53.87, -117.61) * mm, "mid": v(45.18, -117.52) * mm, "end": v(50.9, -124.07) * mm});
            skLineSegment(sketch, "E22.53.0", {"start": v(67.87, -110.13) * mm, "end": v(75.06, -116.32) * mm});
            skLineSegment(sketch, "E22.53.1", {"start": v(75.06, -116.32) * mm, "end": v(65.54, -122.6) * mm});
            skLineSegment(sketch, "E22.53.2", {"start": v(65.54, -122.6) * mm, "end": v(62.81, -118.48) * mm});
            skArc(sketch, "E22.53.3", {"start": v(65.14, -111.76) * mm, "mid": v(67.34, -112.34) * mm, "end": v(67.87, -110.13) * mm});
            skArc(sketch, "E22.53.4", {"start": v(65.14, -111.76) * mm, "mid": v(56.48, -112.53) * mm, "end": v(62.81, -118.48) * mm});
            skLineSegment(sketch, "E22.54.0", {"start": v(78.33, -102.95) * mm, "end": v(86.1, -108.4) * mm});
            skLineSegment(sketch, "E22.54.1", {"start": v(86.1, -108.4) * mm, "end": v(77.24, -115.6) * mm});
            skLineSegment(sketch, "E22.54.2", {"start": v(77.24, -115.6) * mm, "end": v(74.12, -111.76) * mm});
            skArc(sketch, "E22.54.3", {"start": v(75.78, -104.84) * mm, "mid": v(78.02, -105.2) * mm, "end": v(78.33, -102.95) * mm});
            skArc(sketch, "E22.54.4", {"start": v(75.78, -104.84) * mm, "mid": v(67.24, -106.45) * mm, "end": v(74.12, -111.76) * mm});
            skLineSegment(sketch, "E22.55.0", {"start": v(88.05, -94.77) * mm, "end": v(96.3, -99.44) * mm});
            skLineSegment(sketch, "E22.55.1", {"start": v(96.3, -99.44) * mm, "end": v(88.2, -107.47) * mm});
            skLineSegment(sketch, "E22.55.2", {"start": v(88.2, -107.47) * mm, "end": v(84.72, -103.95) * mm});
            skArc(sketch, "E22.55.3", {"start": v(85.7, -96.9) * mm, "mid": v(87.96, -97.04) * mm, "end": v(88.05, -94.77) * mm});
            skArc(sketch, "E22.55.4", {"start": v(85.7, -96.9) * mm, "mid": v(77.35, -99.35) * mm, "end": v(84.72, -103.95) * mm});
            skLineSegment(sketch, "E22.56.0", {"start": v(96.91, -85.69) * mm, "end": v(105.6, -89.52) * mm});
            skLineSegment(sketch, "E22.56.1", {"start": v(105.6, -89.52) * mm, "end": v(98.3, -98.3) * mm});
            skLineSegment(sketch, "E22.56.2", {"start": v(98.3, -98.3) * mm, "end": v(94.5, -95.15) * mm});
            skArc(sketch, "E22.56.3", {"start": v(94.78, -88.04) * mm, "mid": v(97.05, -87.96) * mm, "end": v(96.91, -85.69) * mm});
            skArc(sketch, "E22.56.4", {"start": v(94.78, -88.04) * mm, "mid": v(86.71, -91.29) * mm, "end": v(94.5, -95.15) * mm});
            skLineSegment(sketch, "E22.57.0", {"start": v(104.84, -75.78) * mm, "end": v(113.86, -78.74) * mm});
            skLineSegment(sketch, "E22.57.1", {"start": v(113.86, -78.74) * mm, "end": v(107.47, -88.2) * mm});
            skLineSegment(sketch, "E22.57.2", {"start": v(107.47, -88.2) * mm, "end": v(103.37, -85.43) * mm});
            skArc(sketch, "E22.57.3", {"start": v(102.95, -78.33) * mm, "mid": v(105.2, -78.02) * mm, "end": v(104.84, -75.78) * mm});
            skArc(sketch, "E22.57.4", {"start": v(102.95, -78.33) * mm, "mid": v(95.24, -82.35) * mm, "end": v(103.37, -85.43) * mm});
            skLineSegment(sketch, "E22.58.0", {"start": v(111.77, -65.13) * mm, "end": v(121.03, -67.2) * mm});
            skLineSegment(sketch, "E22.58.1", {"start": v(121.03, -67.2) * mm, "end": v(115.6, -77.24) * mm});
            skLineSegment(sketch, "E22.58.2", {"start": v(115.6, -77.24) * mm, "end": v(111.25, -74.88) * mm});
            skArc(sketch, "E22.58.3", {"start": v(110.13, -67.86) * mm, "mid": v(112.34, -67.33) * mm, "end": v(111.77, -65.13) * mm});
            skArc(sketch, "E22.58.4", {"start": v(110.13, -67.86) * mm, "mid": v(102.86, -72.62) * mm, "end": v(111.25, -74.88) * mm});
            skLineSegment(sketch, "E22.59.0", {"start": v(117.61, -53.87) * mm, "end": v(127.03, -55.01) * mm});
            skLineSegment(sketch, "E22.59.1", {"start": v(127.03, -55.01) * mm, "end": v(122.6, -65.54) * mm});
            skLineSegment(sketch, "E22.59.2", {"start": v(122.6, -65.54) * mm, "end": v(118.05, -63.62) * mm});
            skArc(sketch, "E22.59.3", {"start": v(116.25, -56.74) * mm, "mid": v(118.4, -56) * mm, "end": v(117.61, -53.87) * mm});
            skArc(sketch, "E22.59.4", {"start": v(116.25, -56.74) * mm, "mid": v(109.48, -62.18) * mm, "end": v(118.05, -63.62) * mm});
            skLineSegment(sketch, "E22.60.0", {"start": v(122.33, -42.08) * mm, "end": v(131.81, -42.3) * mm});
            skLineSegment(sketch, "E22.60.1", {"start": v(131.81, -42.3) * mm, "end": v(128.44, -53.2) * mm});
            skLineSegment(sketch, "E22.60.2", {"start": v(128.44, -53.2) * mm, "end": v(123.72, -51.74) * mm});
            skArc(sketch, "E22.60.3", {"start": v(121.26, -45.07) * mm, "mid": v(123.32, -44.12) * mm, "end": v(122.33, -42.08) * mm});
            skArc(sketch, "E22.60.4", {"start": v(121.26, -45.07) * mm, "mid": v(115.05, -51.15) * mm, "end": v(123.72, -51.74) * mm});
            skLineSegment(sketch, "E22.61.0", {"start": v(125.86, -29.89) * mm, "end": v(135.32, -29.17) * mm});
            skLineSegment(sketch, "E22.61.1", {"start": v(135.32, -29.17) * mm, "end": v(133.04, -40.36) * mm});
            skLineSegment(sketch, "E22.61.2", {"start": v(133.04, -40.36) * mm, "end": v(128.2, -39.37) * mm});
            skArc(sketch, "E22.61.3", {"start": v(125.09, -32.97) * mm, "mid": v(127.05, -31.82) * mm, "end": v(125.86, -29.89) * mm});
            skArc(sketch, "E22.61.4", {"start": v(125.09, -32.97) * mm, "mid": v(119.5, -39.63) * mm, "end": v(128.2, -39.37) * mm});
            skLineSegment(sketch, "E22.62.0", {"start": v(128.18, -17.4) * mm, "end": v(137.53, -15.77) * mm});
            skLineSegment(sketch, "E22.62.1", {"start": v(137.53, -15.77) * mm, "end": v(136.35, -27.12) * mm});
            skLineSegment(sketch, "E22.62.2", {"start": v(136.35, -27.12) * mm, "end": v(131.44, -26.61) * mm});
            skArc(sketch, "E22.62.3", {"start": v(127.72, -20.55) * mm, "mid": v(129.56, -19.22) * mm, "end": v(128.18, -17.4) * mm});
            skArc(sketch, "E22.62.4", {"start": v(127.72, -20.55) * mm, "mid": v(122.82, -27.73) * mm, "end": v(131.44, -26.61) * mm});
            skLineSegment(sketch, "E22.63.0", {"start": v(129.27, -4.76) * mm, "end": v(138.41, -2.21) * mm});
            skLineSegment(sketch, "E22.63.1", {"start": v(138.41, -2.21) * mm, "end": v(138.35, -13.63) * mm});
            skLineSegment(sketch, "E22.63.2", {"start": v(138.35, -13.63) * mm, "end": v(133.41, -13.6) * mm});
            skArc(sketch, "E22.63.3", {"start": v(129.12, -7.93) * mm, "mid": v(130.82, -6.42) * mm, "end": v(129.27, -4.76) * mm});
            skArc(sketch, "E22.63.4", {"start": v(129.12, -7.93) * mm, "mid": v(124.94, -15.56) * mm, "end": v(133.41, -13.6) * mm});
            skCircle(sketch, "E23.1.0", {"center": v(37.32, -51.37) * mm, "radius": 5.24 * mm});
            skCircle(sketch, "E23.2.0", {"center": v(-37.32, -51.37) * mm, "radius": 5.24 * mm});
            skCircle(sketch, "E23.3.0", {"center": v(-60.4, 19.62) * mm, "radius": 5.24 * mm});
            skCircle(sketch, "E23.4.0", {"center": v(0, 63.5) * mm, "radius": 5.24 * mm});
            skLineSegment(sketch, "E23.anchor1", {"start": v(0, 0) * mm, "end": v(60.4, 19.62) * mm, "construction": true});
            skLineSegment(sketch, "E23.anchor2", {"start": v(0, 0) * mm, "end": v(0, 63.5) * mm, "construction": true});
            skSolve(sketch);
        }
        {
            var Q0;
            Q0=makeQuery(id+"F0.imprint","IMPRINT",FACE,{"disambiguationData":[TD([[makeQuery(id+"F0.imprint","IMPRINT",EDGE,{"derivedFrom":sQuery(id+"F0.wireOp",EDGE,"E1")}),-1.0]])]});
            extrude(context, id + "F1", {"entities" : qUnion([Q0]), "endBound" : BoundingType.SYMMETRIC, "depth" : 1.59 * mm});
        }
        {
            var Q0;
            Q0=qCreatedBy(makeId("Top.planeOp"),FACE);
            var sketch = newSketch(context, id + "F2", { "sketchPlane" : qUnion([Q0])});
            skCircle(sketch, "E24", {"center": v(-130.78, 38.9) * mm, "radius": 38.5 * mm});
            skCircle(sketch, "E25.MirrorC", {"center": v(-130.78, -38.9) * mm, "radius": 38.5 * mm});
            skLineSegment(sketch, "E26", {"start": v(0, 75.17) * mm, "end": v(0, -72.2) * mm});
            skSolve(sketch);
        }
        {
            var Q0;
            Q0=makeQuery(id+"F2.imprint","IMPRINT",FACE,{"disambiguationData":[TD([[makeQuery(id+"F2.imprint","IMPRINT",EDGE,{"derivedFrom":sQuery(id+"F2.wireOp",EDGE,"E24")}),1.0]])]});
            var Q1;
            Q1=makeQuery(id+"F2.imprint","IMPRINT",FACE,{"disambiguationData":[TD([[makeQuery(id+"F2.imprint","IMPRINT",EDGE,{"derivedFrom":sQuery(id+"F2.wireOp",EDGE,"E25.MirrorC")}),-1.0]])]});
            var Q2;
            Q2=sQuery(id+"F2.wireOp",EDGE,"E26");
            revolve(context, id + "F3", {"operationType" : NewBodyOperationType.REMOVE, "entities" : qUnion([Q0, Q1]), "axis" : qUnion([Q2]), "revolveType" : RevolveType.FULL, "oppositeDirection" : true});
        }
    });
